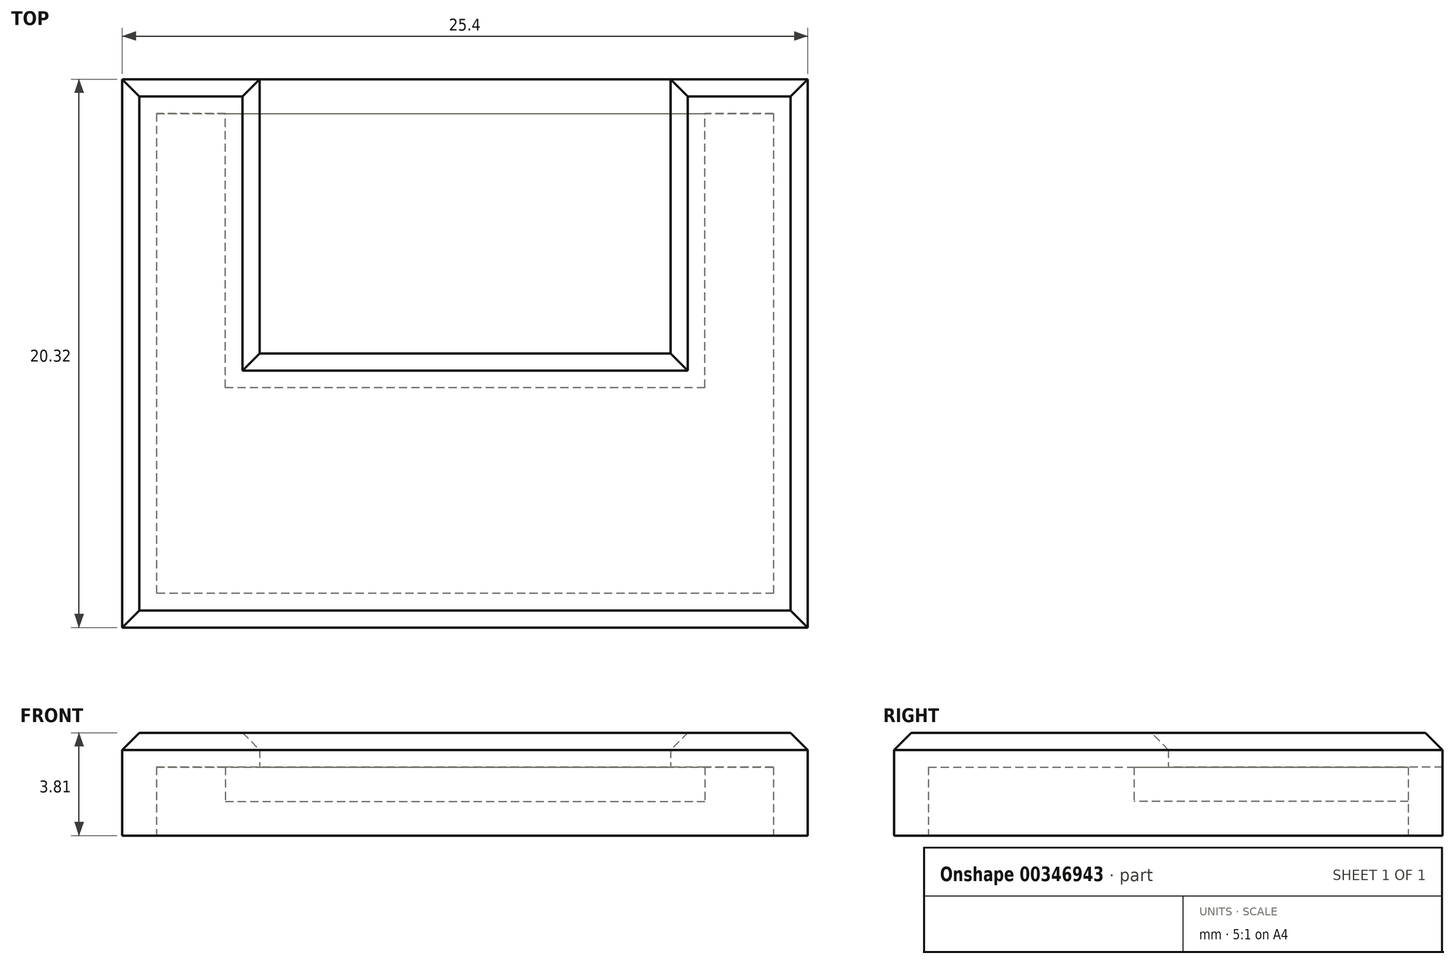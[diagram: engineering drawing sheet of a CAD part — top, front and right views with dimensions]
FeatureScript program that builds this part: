
annotation { "Feature Type Name" : "Feature", "Feature Type Description" : "" }
export const myFeature = defineFeature(function(context is Context, id is Id, definition is map)
    precondition{}
    {
        {
            var Q0;
            Q0=qCreatedBy(makeId("Top.planeOp"),FACE);
            var sketch = newSketch(context, id + "F0", { "sketchPlane" : qUnion([Q0])});
            skLineSegment(sketch, "E0.bottom", {"start": v(0, 0) * mm, "end": v(-25.4, 0) * mm});
            skLineSegment(sketch, "E0.top", {"start": v(0, -25.4) * mm, "end": v(-25.4, -25.4) * mm});
            skLineSegment(sketch, "E0.left", {"start": v(0, 0) * mm, "end": v(0, -25.4) * mm});
            skLineSegment(sketch, "E0.right", {"start": v(-25.4, 0) * mm, "end": v(-25.4, -25.4) * mm});
            skLineSegment(sketch, "E1.bottom", {"start": v(-25.4, 0) * mm, "end": v(0, 0) * mm});
            skLineSegment(sketch, "E1.top", {"start": v(-25.4, -5.08) * mm, "end": v(0, -5.08) * mm});
            skLineSegment(sketch, "E1.left", {"start": v(-25.4, 0) * mm, "end": v(-25.4, -5.08) * mm});
            skLineSegment(sketch, "E1.right", {"start": v(0, 0) * mm, "end": v(0, -5.08) * mm});
            skLineSegment(sketch, "E2.top", {"start": v(-25.4, -15.24) * mm, "end": v(0, -15.24) * mm});
            skLineSegment(sketch, "E2.left", {"start": v(-25.4, -5.08) * mm, "end": v(-25.4, -15.24) * mm});
            skLineSegment(sketch, "E2.right", {"start": v(0, -5.08) * mm, "end": v(0, -15.24) * mm});
            skLineSegment(sketch, "E3.bottom", {"start": v(-25.4, 0) * mm, "end": v(-20.3, 0) * mm});
            skLineSegment(sketch, "E3.top", {"start": v(-25.4, -25.4) * mm, "end": v(-20.3, -25.4) * mm});
            skLineSegment(sketch, "E3.right", {"start": v(-20.3, 0) * mm, "end": v(-20.3, -25.4) * mm});
            skLineSegment(sketch, "E4.bottom", {"start": v(0, 0) * mm, "end": v(-5.08, 0) * mm});
            skLineSegment(sketch, "E4.top", {"start": v(0, -25.4) * mm, "end": v(-5.08, -25.4) * mm});
            skLineSegment(sketch, "E4.right", {"start": v(-5.08, 0) * mm, "end": v(-5.08, -25.4) * mm});
            skSolve(sketch);
        }
        {
            var Q0;
            {var subQ5=sQuery(id+"F0.wireOp",EDGE,"E3.bottom");Q0=makeQuery(id+"F0.imprint","IMPRINT",FACE,{"disambiguationData":[TD([[makeQuery(id+"F0.imprint","IMPRINT",EDGE,{"derivedFrom":subQ5}),-1.0]])]});}
            var Q1;
            {var subQ0=sQuery(id+"F0.wireOp",EDGE,"E1.bottom");Q1=makeQuery(id+"F0.imprint","IMPRINT",FACE,{"disambiguationData":[TD([[makeQuery(id+"F0.imprint","IMPRINT",EDGE,{"derivedFrom":subQ0}),-1.0]])]});}
            var Q2;
            {var subQ5=sQuery(id+"F0.wireOp",EDGE,"E4.bottom");Q2=makeQuery(id+"F0.imprint","IMPRINT",FACE,{"disambiguationData":[TD([[makeQuery(id+"F0.imprint","IMPRINT",EDGE,{"derivedFrom":subQ5}),1.0]])]});}
            var Q3;
            {var subQ0=sQuery(id+"F0.wireOp",EDGE,"E0.left");var subQ1=sQuery(id+"F0.wireOp",EDGE,"E1.top");var subQ2=makeQuery(id+"F0.imprint","INTERSECT",VERTEX,{"derivedFrom":[subQ1,subQ0]});Q3=makeQuery(id+"F0.imprint","IMPRINT",FACE,{"disambiguationData":[TD([[makeQuery(id+"F0.imprint","IMPRINT",EDGE,{"disambiguationData":[TD([[subQ2,1.0]])],"derivedFrom":subQ1}),-1.0]])]});}
            var Q4;
            {var subQ0=sQuery(id+"F0.wireOp",EDGE,"E0.right");var subQ1=sQuery(id+"F0.wireOp",EDGE,"E1.top");var subQ2=makeQuery(id+"F0.imprint","INTERSECT",VERTEX,{"derivedFrom":[subQ1,subQ0]});Q4=makeQuery(id+"F0.imprint","IMPRINT",FACE,{"disambiguationData":[TD([[makeQuery(id+"F0.imprint","IMPRINT",EDGE,{"disambiguationData":[TD([[subQ2,-1.0]])],"derivedFrom":subQ1}),-1.0]])]});}
            var Q5;
            {var subQ5=sQuery(id+"F0.wireOp",EDGE,"E3.top");Q5=makeQuery(id+"F0.imprint","IMPRINT",FACE,{"disambiguationData":[TD([[makeQuery(id+"F0.imprint","IMPRINT",EDGE,{"derivedFrom":subQ5}),1.0]])]});}
            var Q6;
            {var subQ0=sQuery(id+"F0.wireOp",EDGE,"E0.top");Q6=makeQuery(id+"F0.imprint","IMPRINT",FACE,{"disambiguationData":[TD([[makeQuery(id+"F0.imprint","IMPRINT",EDGE,{"derivedFrom":subQ0}),-1.0]])]});}
            var Q7;
            {var subQ5=sQuery(id+"F0.wireOp",EDGE,"E4.top");Q7=makeQuery(id+"F0.imprint","IMPRINT",FACE,{"disambiguationData":[TD([[makeQuery(id+"F0.imprint","IMPRINT",EDGE,{"derivedFrom":subQ5}),-1.0]])]});}
            extrude(context, id + "F1", {"entities" : qUnion([Q0, Q1, Q2, Q3, Q4, Q5, Q6, Q7]), "depth" : 3.8 * mm});
        }
        {
            var Q0;
            {var subQ0=sQuery(id+"F0.wireOp",EDGE,"E3.right");var subQ1=sQuery(id+"F0.wireOp",EDGE,"E1.top");var subQ2=makeQuery(id+"F0.imprint","INTERSECT",VERTEX,{"derivedFrom":[subQ1,subQ0]});Q0=makeQuery(id+"F0.imprint","IMPRINT",FACE,{"disambiguationData":[TD([[makeQuery(id+"F0.imprint","IMPRINT",EDGE,{"disambiguationData":[TD([[subQ2,-1.0]])],"derivedFrom":subQ1}),-1.0]])]});}
            extrude(context, id + "F2", {"entities" : qUnion([Q0]), "operationType" : NewBodyOperationType.ADD, "depth" : 2.54 * mm});
        }
        {
            var Q0;
            Q0=makeQuery(id+"F1.opExtrude","CAP_EDGE",EDGE,{"disambiguationData":[OSD([sQuery(id+"F0.wireOp",EDGE,"E1.top")])],"isStart":false});
            var Q1;
            Q1=makeQuery(id+"F1.opExtrude","CAP_EDGE",EDGE,{"disambiguationData":[OSD([sQuery(id+"F0.wireOp",EDGE,"E4.right")])],"isStart":false});
            var Q2;
            Q2=makeQuery(id+"F1.opExtrude","CAP_EDGE",EDGE,{"disambiguationData":[OSD([sQuery(id+"F0.wireOp",EDGE,"E3.right")])],"isStart":false});
            var Q3;
            Q3=makeQuery(id+"F1.opExtrude","CAP_EDGE",EDGE,{"disambiguationData":[OSD([sQuery(id+"F0.wireOp",EDGE,"E2.top")])],"isStart":false});
            chamfer(context, id + "F3", {"entities" : qUnion([Q0, Q1, Q2, Q3]), "width" : 0.64 * mm, "tangentPropagation" : true});
        }
        {
            var Q0;
            Q0=makeQuery(id+"F1.opExtrude","CAP_EDGE",EDGE,{"disambiguationData":[OSD([sQuery(id+"F0.wireOp",EDGE,"E1.bottom"),sQuery(id+"F0.wireOp",EDGE,"E3.bottom"),sQuery(id+"F0.wireOp",EDGE,"E4.bottom")])],"isStart":false});
            var Q1;
            Q1=makeQuery(id+"F1.opExtrude","CAP_EDGE",EDGE,{"disambiguationData":[OSD([sQuery(id+"F0.wireOp",EDGE,"E0.left")])],"isStart":false});
            var Q2;
            Q2=makeQuery(id+"F1.opExtrude","CAP_EDGE",EDGE,{"disambiguationData":[OSD([sQuery(id+"F0.wireOp",EDGE,"E0.right")])],"isStart":false});
            var Q3;
            Q3=makeQuery(id+"F1.opExtrude","CAP_EDGE",EDGE,{"disambiguationData":[OSD([sQuery(id+"F0.wireOp",EDGE,"E0.top"),sQuery(id+"F0.wireOp",EDGE,"E3.top"),sQuery(id+"F0.wireOp",EDGE,"E4.top")])],"isStart":false});
            chamfer(context, id + "F4", {"entities" : qUnion([Q0, Q1, Q2, Q3]), "width" : 0.64 * mm, "tangentPropagation" : true});
        }
        {
            var Q0;
            {var subQ0=sQuery(id+"F0.wireOp",EDGE,"E4.right");var subQ1=sQuery(id+"F0.wireOp",EDGE,"E3.right");var subQ2=sQuery(id+"F0.wireOp",EDGE,"E2.top");var subQ3=sQuery(id+"F0.wireOp",EDGE,"E1.top");Q0=makeQuery(id+"F2.boolean.opBoolean","MERGE",FACE,{"derivedFrom":[makeQuery(id+"F1.opExtrude","CAP_FACE",FACE,{"disambiguationData":[OSD([sQuery(id+"F0.wireOp",EDGE,"E0.top"),sQuery(id+"F0.wireOp",EDGE,"E1.bottom"),subQ3,subQ2,sQuery(id+"F0.wireOp",EDGE,"E3.bottom"),sQuery(id+"F0.wireOp",EDGE,"E3.top"),sQuery(id+"F0.wireOp",EDGE,"E0.right"),subQ1,sQuery(id+"F0.wireOp",EDGE,"E4.bottom"),sQuery(id+"F0.wireOp",EDGE,"E4.top"),sQuery(id+"F0.wireOp",EDGE,"E0.left"),subQ0])],"isStart":true}),makeQuery(id+"F2.opExtrude","CAP_FACE",FACE,{"disambiguationData":[OSD([subQ3,subQ2,subQ1,subQ0])],"isStart":true})]});}
            shell(context, id + "F5", {"entities" : qUnion([Q0]), "thickness" : 1.27 * mm});
        }
    });
